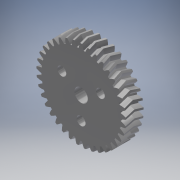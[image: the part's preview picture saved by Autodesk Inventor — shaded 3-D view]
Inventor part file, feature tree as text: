
AUTODESK INVENTOR PART (.ipt)
format: ipt  version: 2019 (Build 230136000, 136)  size: 913,920 bytes
history: native  units: mm (DEFAULTED — no unit token found)
features: sketch x4, plane x3, other x3, extrude x2, mirror x1, hole x1
ambient origin geometry x8: Origin, YZ Plane, XZ Plane, XY Plane, X Axis, Y Axis, Z Axis, Center Point
bodies: Solid1 (feature_tree)
feature tree (14):
  extrude  "Extrusion1"  Depth=5.0mm TaperAngle=0.0deg
  plane  "Work Plane2"
  plane  "Work Plane8"
  plane  "Work Plane9"
  other  "Spur Gear"
  mirror  "Mirror1"
  extrude  "Extrusion4"  Depth=10.0mm TaperAngle=0.0deg
  hole  "Hole3"  [1 undecoded]
  sketch  "Sketch1"  dims[d0=50.240958mm d1=5.0mm d2=0.0mm]
  sketch  "Sketch2"  dims[d3=47.741935mm d4=10.0mm d5=0.0mm]
  other  "Srf1"
  sketch  "Sketch6"  dims[d16=40.0mm d17=0.0mm d34=0.849079mm]
  sketch  "Sketch8"  dims[d39=0.0mm d41=0.0mm d43=40.0mm d46=40.0mm d47=0.0mm d48=0.0mm d66=7.5mm d67=5.0mm d68=0.0mm d81=30.0mm d83=360.0deg d85=5.0mm d86=6.0mm d87=8.0mm d88=7.0mm d89=90.0deg d90=8.0mm d91=20.594885mm]
  other  "Pitch Diameter"
note: 1 required parameter value undecoded (feature->parameter linkage not recoverable at this tier; creation-order binding heuristic only, values carry confidence <= 0.55)
